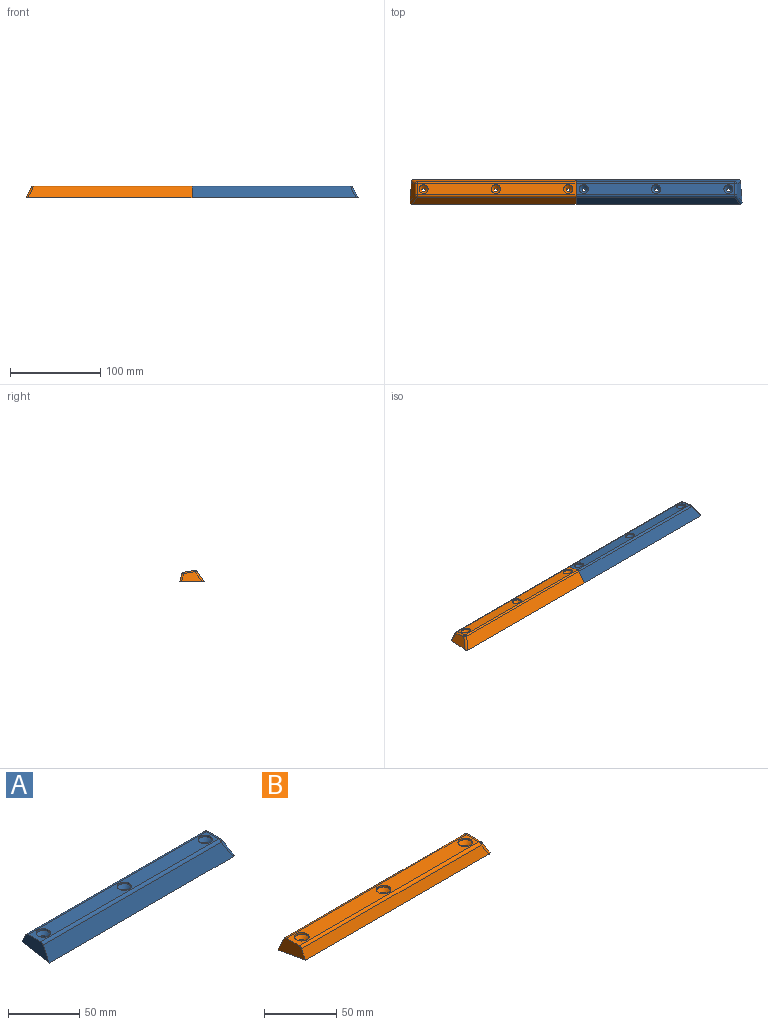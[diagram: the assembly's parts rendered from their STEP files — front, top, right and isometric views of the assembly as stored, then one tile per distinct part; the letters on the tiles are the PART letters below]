
ASSEMBLY  parts=2 mates=1
PART A: 22 faces, bbox 184.7x27.3x14.5 mm
  f0: cylinder r=2.38mm len=7.92mm, axis (0,0,1), area 112.4mm2, adj f7,f20
  f1: cylinder r=2.38mm len=7.92mm, axis (0,0,1), area 112.4mm2, adj f7,f21
  f2: cylinder r=2.38mm len=7.92mm, axis (0,0,1), area 112.4mm2, adj f7,f19
  f3: plane 22.2x12.21mm, normal (0.91,0,0.42), area 195.1mm2, adj f7,f10,f13,f15
  f4: plane 182.08x12.65mm, normal (0,-0.91,0.42), area 2501mm2, adj f5,f7,f9,f10
  f5: plane 26.84x14.12mm, normal (-1,0,0), area 247.5mm2, adj f4,f6,f7,f8,f9,f12
  f6: plane 179.88x7.92mm, normal (0,0.91,0.42), area 1556.1mm2, adj f5,f7,f12,f15
  f7: plane 184.37x27.01mm, normal (0,0.17,-0.98), area 4938.1mm2, adj f0,f1,f2,f3,f4,f5,f6,f10
  f8: plane 176.18x12.64mm, normal (0,0,1), area 1983.5mm2, adj f5,f9,f12,f13,f16,f17,f18
  f9: cylinder r=2.54mm len=176.18mm, axis (-1,0,0), area 507.7mm2, adj f4,f5,f8,f11
  f10: cylinder r=2.54mm len=13.21mm, axis (-0.39,0.39,0.83), area 53.8mm2, adj f3,f4,f7,f11
  f11: sphere r=2.54mm, area 5mm2, adj f9,f10,f13
  f12: cylinder r=2.54mm len=176.18mm, axis (-1,0,0), area 507.7mm2, adj f5,f6,f8,f14
  f13: cylinder r=2.54mm len=12.64mm, axis (0,1,0), area 36.4mm2, adj f3,f8,f11,f14
  f14: sphere r=2.54mm, area 5mm2, adj f12,f13,f15
  f15: cylinder r=2.54mm len=8.72mm, axis (-0.39,-0.39,0.83), area 35mm2, adj f3,f6,f7,f14
  f16: cylinder r=5.08mm len=10.16mm, axis (0,0,1), area 43.6mm2, adj f8,f21
  f17: cylinder r=5.08mm len=10.16mm, axis (0,0,1), area 43.6mm2, adj f8,f20
  f18: cylinder r=5.08mm len=10.16mm, axis (0,0,1), area 43.6mm2, adj f8,f19
  f19: cone r=2.38mm half-angle=45deg, axis (0,0,1), area 89.5mm2, adj f2,f18
  f20: cone r=2.38mm half-angle=45deg, axis (0,0,1), area 89.5mm2, adj f0,f17
  f21: cone r=2.38mm half-angle=45deg, axis (0,0,1), area 89.5mm2, adj f1,f16
PART B: 22 faces, bbox 184.7x27.3x14.5 mm
  f0: cylinder r=2.38mm len=7.92mm, axis (0,0,1), area 112.4mm2, adj f7,f20
  f1: cylinder r=2.38mm len=7.92mm, axis (0,0,1), area 112.4mm2, adj f7,f21
  f2: cylinder r=2.38mm len=7.92mm, axis (0,0,1), area 112.4mm2, adj f7,f19
  f3: plane 22.2x12.21mm, normal (0.91,0,0.42), area 195.1mm2, adj f7,f10,f13,f15
  f4: plane 182.08x12.65mm, normal (0,0.91,0.42), area 2501mm2, adj f5,f7,f9,f10
  f5: plane 26.84x14.12mm, normal (-1,0,0), area 247.5mm2, adj f4,f6,f7,f8,f9,f12
  f6: plane 179.88x7.92mm, normal (0,-0.91,0.42), area 1556.1mm2, adj f5,f7,f12,f15
  f7: plane 184.37x27.01mm, normal (0,-0.17,-0.98), area 4938.1mm2, adj f0,f1,f2,f3,f4,f5,f6,f10
  f8: plane 176.18x12.64mm, normal (0,0,1), area 1983.5mm2, adj f5,f9,f12,f13,f16,f17,f18
  f9: cylinder r=2.54mm len=176.18mm, axis (-1,0,0), area 507.7mm2, adj f4,f5,f8,f11
  f10: cylinder r=2.54mm len=13.21mm, axis (-0.39,-0.39,0.83), area 53.8mm2, adj f3,f4,f7,f11
  f11: sphere r=2.54mm, area 5mm2, adj f9,f10,f13
  f12: cylinder r=2.54mm len=176.18mm, axis (-1,0,0), area 507.7mm2, adj f5,f6,f8,f14
  f13: cylinder r=2.54mm len=12.64mm, axis (0,-1,0), area 36.4mm2, adj f3,f8,f11,f14
  f14: sphere r=2.54mm, area 5mm2, adj f12,f13,f15
  f15: cylinder r=2.54mm len=8.72mm, axis (-0.39,0.39,0.83), area 35mm2, adj f3,f6,f7,f14
  f16: cylinder r=5.08mm len=10.16mm, axis (0,0,1), area 43.6mm2, adj f8,f21
  f17: cylinder r=5.08mm len=10.16mm, axis (0,0,1), area 43.6mm2, adj f8,f20
  f18: cylinder r=5.08mm len=10.16mm, axis (0,0,1), area 43.6mm2, adj f8,f19
  f19: cone r=2.38mm half-angle=45deg, axis (0,0,1), area 89.5mm2, adj f2,f18
  f20: cone r=2.38mm half-angle=45deg, axis (0,0,1), area 89.5mm2, adj f0,f17
  f21: cone r=2.38mm half-angle=45deg, axis (0,0,1), area 89.5mm2, adj f1,f16
PLACE A rot(axis=(-1,0,0),10deg) t=(177.8,-18.38,14.98)mm
PLACE B rot(axis=(0,0.09,1),180deg) t=(0,67.67,-0.19)mm
MATE fastened B.f12 <-> A.f12  axis (1,0,0) through (88.9,7.79,7.79)mm
